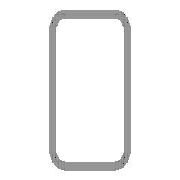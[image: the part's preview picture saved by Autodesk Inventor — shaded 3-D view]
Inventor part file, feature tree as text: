
AUTODESK INVENTOR PART (.ipt)
format: ipt  version: 2025 (Build 290162010, 162A)  size: 134,144 bytes
history: native  units: mm (DEFAULTED — no unit token found)
features: other x4, sketch x1, plane x1
ambient origin geometry x8: Origin, YZ Plane, XZ Plane, XY Plane, X Axis, Y Axis, Z Axis, Center Point
bodies: Solid1 (feature_tree), Body (feature_tree)
feature tree (6):
  parser-record x1  (decoder bookkeeping rows leaked as tree rows — omitted from the tree; the rows remain in map.json)
  other  "Driven Length"
  other  "Start Plane"
  other  "End Plane"
  sketch  "Sketch3"  dims[d3=320.0mm d4=0.0mm d7=4.0mm d9=20.0mm d11=40.0mm d12=2.0mm d13=40.0mm d14=360.0mm d15=10.0mm d16=20.0mm d17=90.0deg d18=320.0mm]
  plane  "Work Plane3"
